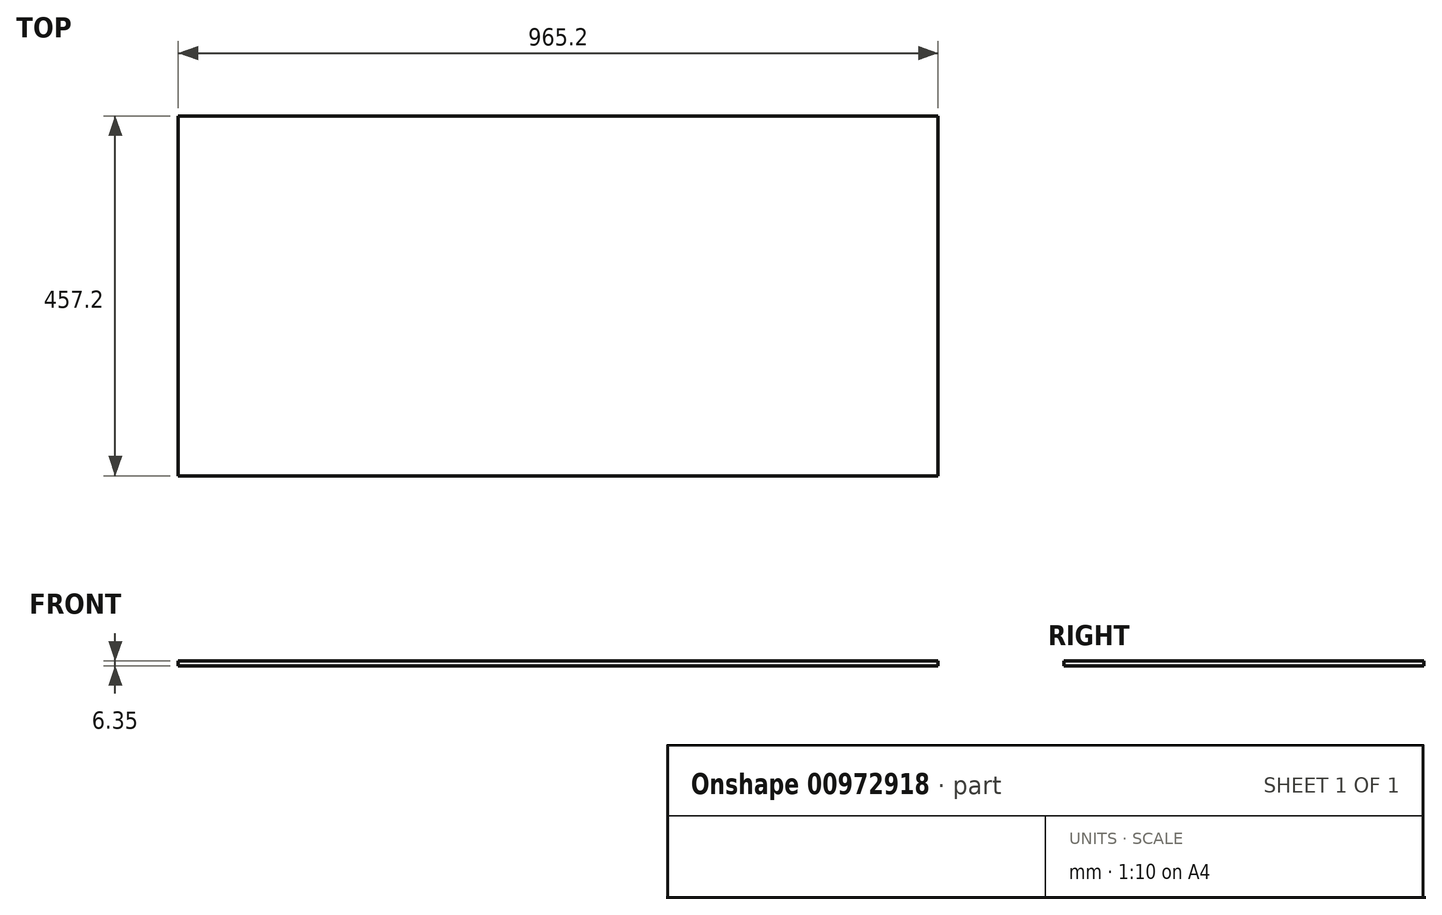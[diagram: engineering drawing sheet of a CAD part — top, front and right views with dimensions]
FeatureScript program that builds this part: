
annotation { "Feature Type Name" : "Feature", "Feature Type Description" : "" }
export const myFeature = defineFeature(function(context is Context, id is Id, definition is map)
    precondition{}
    {
        {
            var Q0;
            Q0=qCreatedBy(makeId("Top.planeOp"),FACE);
            var sketch = newSketch(context, id + "F0", { "sketchPlane" : qUnion([Q0])});
            skLineSegment(sketch, "E0.bottom", {"start": v(-434.66, 258.07) * mm, "end": v(530.54, 258.07) * mm});
            skLineSegment(sketch, "E0.top", {"start": v(-434.66, -199.13) * mm, "end": v(530.54, -199.13) * mm});
            skLineSegment(sketch, "E0.left", {"start": v(-434.66, 258.07) * mm, "end": v(-434.66, -199.13) * mm});
            skLineSegment(sketch, "E0.right", {"start": v(530.54, 258.07) * mm, "end": v(530.54, -199.13) * mm});
            skSolve(sketch);
        }
        {
            var Q0;
            Q0=makeQuery(id+"F0.imprint","IMPRINT",FACE,{"disambiguationData":[TD([[makeQuery(id+"F0.imprint","IMPRINT",EDGE,{"derivedFrom":sQuery(id+"F0.wireOp",EDGE,"E0.bottom")}),-1.0]])]});
            extrude(context, id + "F1", {"entities" : qUnion([Q0]), "depth" : 6.35 * mm, "offsetDistance" : 25.4 * mm});
        }
    });
